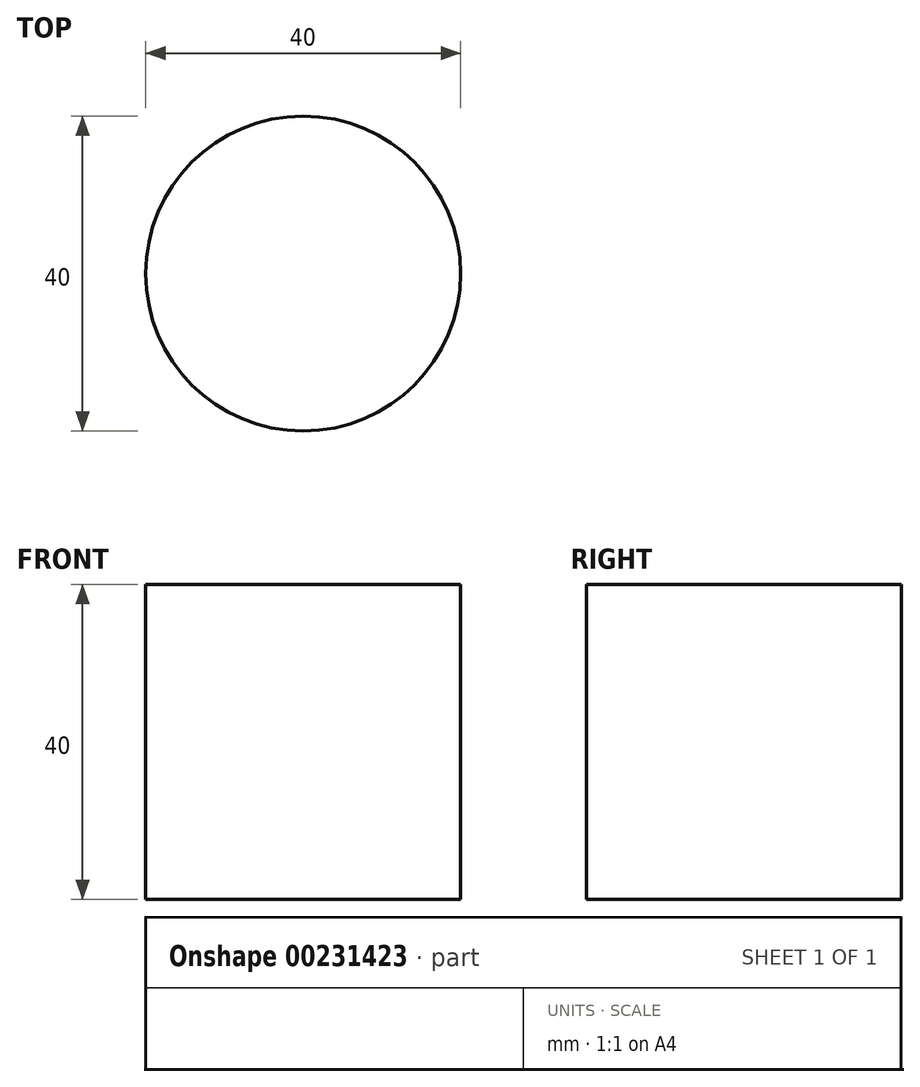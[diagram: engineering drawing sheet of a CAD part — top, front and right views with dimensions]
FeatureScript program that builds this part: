
annotation { "Feature Type Name" : "Feature", "Feature Type Description" : "" }
export const myFeature = defineFeature(function(context is Context, id is Id, definition is map)
    precondition{}
    {
        {
            var Q0;
            Q0=qCreatedBy(makeId("Front.planeOp"),FACE);
            var sketch = newSketch(context, id + "F0", { "sketchPlane" : qUnion([Q0])});
            skLineSegment(sketch, "E0.bottom", {"start": v(0, 0) * mm, "end": v(20, 0) * mm});
            skLineSegment(sketch, "E0.top", {"start": v(0, 40) * mm, "end": v(20, 40) * mm});
            skLineSegment(sketch, "E0.left", {"start": v(0, 0) * mm, "end": v(0, 40) * mm});
            skLineSegment(sketch, "E0.right", {"start": v(20, 0) * mm, "end": v(20, 40) * mm});
            skSolve(sketch);
        }
        {
            var Q0;
            Q0=makeQuery(id+"F0.imprint","IMPRINT",FACE,{"disambiguationData":[TD([[makeQuery(id+"F0.imprint","IMPRINT",EDGE,{"derivedFrom":sQuery(id+"F0.wireOp",EDGE,"E0.bottom")}),1.0]])]});
            var Q1;
            Q1=sQuery(id+"F0.wireOp",EDGE,"E0.left");
            revolve(context, id + "F1", {"entities" : qUnion([Q0]), "axis" : qUnion([Q1]), "revolveType" : RevolveType.FULL});
        }
    });
